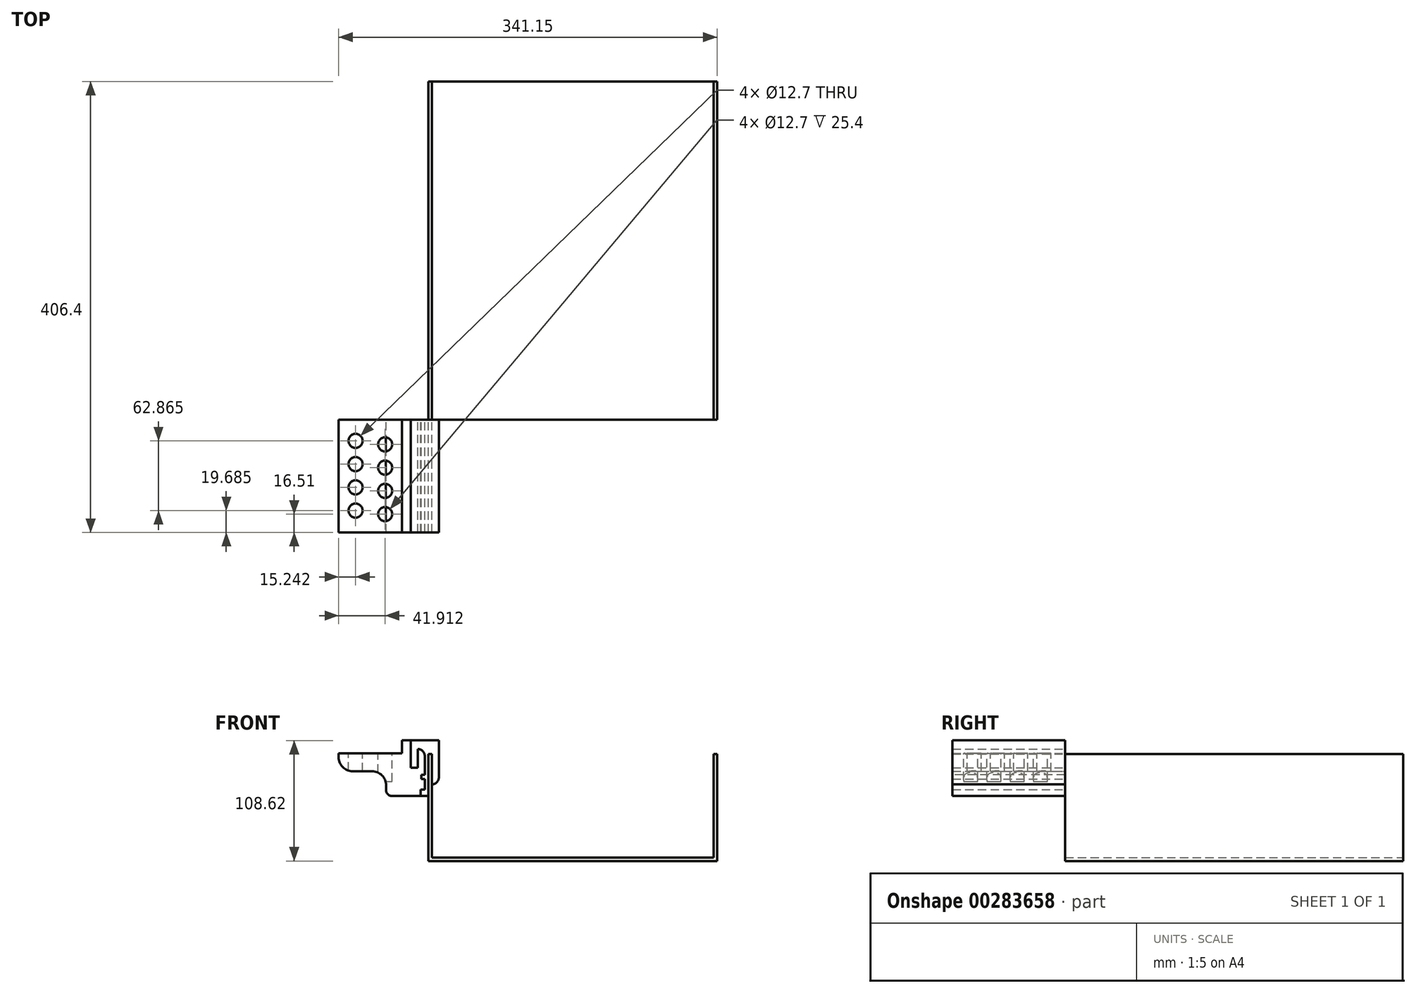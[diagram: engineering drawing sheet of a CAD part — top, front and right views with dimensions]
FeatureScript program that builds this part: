
annotation { "Feature Type Name" : "Feature", "Feature Type Description" : "" }
export const myFeature = defineFeature(function(context is Context, id is Id, definition is map)
    precondition{}
    {
        {
            var Q0;
            Q0=qCreatedBy(makeId("Front.planeOp"),FACE);
            var sketch = newSketch(context, id + "F0", { "sketchPlane" : qUnion([Q0])});
            skLineSegment(sketch, "E0", {"start": v(0, 84.47) * mm, "end": v(0, -105.43) * mm, "construction": true});
            skLineSegment(sketch, "E1", {"start": v(-72.49, 0) * mm, "end": v(75.48, 0) * mm, "construction": true});
            skLineSegment(sketch, "E2", {"start": v(-130.17, 36.54) * mm, "end": v(-130.17, -59.9) * mm});
            skLineSegment(sketch, "E3", {"start": v(-130.17, -59.9) * mm, "end": v(0, -59.9) * mm});
            skLineSegment(sketch, "E4", {"start": v(-130.17, 36.54) * mm, "end": v(-127, 36.54) * mm});
            skLineSegment(sketch, "E5", {"start": v(-127, 36.54) * mm, "end": v(-127, -56.73) * mm});
            skLineSegment(sketch, "E6", {"start": v(-127, -56.73) * mm, "end": v(0, -56.73) * mm});
            skLineSegment(sketch, "E7.MirrorCS", {"start": v(130.17, 36.54) * mm, "end": v(127, 36.54) * mm});
            skLineSegment(sketch, "E8.MirrorCS", {"start": v(130.17, -59.9) * mm, "end": v(0, -59.9) * mm});
            skLineSegment(sketch, "E9.MirrorCS", {"start": v(130.17, 36.54) * mm, "end": v(130.17, -59.9) * mm});
            skLineSegment(sketch, "E10.MirrorCS", {"start": v(127, 36.54) * mm, "end": v(127, -56.73) * mm});
            skLineSegment(sketch, "E11.MirrorCS", {"start": v(127, -56.73) * mm, "end": v(0, -56.73) * mm});
            skSolve(sketch);
        }
        {
            var Q0;
            Q0 = qSketchRegion(id + "F0", true);
            extrude(context, id + "F1", {"entities" : qUnion([Q0]), "depth" : 304.8 * mm});
        }
        {
            var Q0;
            Q0=makeQuery(id+"F1.opExtrude","CAP_FACE",FACE,{"disambiguationData":[OSD([sQuery(id+"F0.wireOp",EDGE,"E2"),sQuery(id+"F0.wireOp",EDGE,"E3"),sQuery(id+"F0.wireOp",EDGE,"E4"),sQuery(id+"F0.wireOp",EDGE,"E5"),sQuery(id+"F0.wireOp",EDGE,"E6"),sQuery(id+"F0.wireOp",EDGE,"E7.MirrorCS"),sQuery(id+"F0.wireOp",EDGE,"E8.MirrorCS"),sQuery(id+"F0.wireOp",EDGE,"E9.MirrorCS"),sQuery(id+"F0.wireOp",EDGE,"E10.MirrorCS"),sQuery(id+"F0.wireOp",EDGE,"E11.MirrorCS")])],"isStart":false});
            var sketch = newSketch(context, id + "F2", { "sketchPlane" : qUnion([Q0])});
            skLineSegment(sketch, "E12", {"start": v(-127, 9.13) * mm, "end": v(-127, 9.13) * mm});
            skLineSegment(sketch, "E13", {"start": v(-120.65, 15.48) * mm, "end": v(-120.65, 48.71) * mm});
            skLineSegment(sketch, "E14", {"start": v(-120.65, 48.71) * mm, "end": v(-146.05, 48.71) * mm});
            skLineSegment(sketch, "E15", {"start": v(-146.05, 48.71) * mm, "end": v(-146.05, 24) * mm});
            skLineSegment(sketch, "E16", {"start": v(-127, 36.54) * mm, "end": v(-127, 9.13) * mm});
            skLineSegment(sketch, "E17", {"start": v(-133.35, 34.7) * mm, "end": v(-133.35, 4.57) * mm});
            skLineSegment(sketch, "E18", {"start": v(-133.35, 4.57) * mm, "end": v(-136.96, 4.57) * mm});
            skLineSegment(sketch, "E19", {"start": v(-136.96, 4.57) * mm, "end": v(-136.96, -1.3) * mm});
            skLineSegment(sketch, "E20", {"start": v(-136.96, -1.3) * mm, "end": v(-130.17, -1.3) * mm});
            skLineSegment(sketch, "E21", {"start": v(-130.17, -1.3) * mm, "end": v(-130.17, 36.54) * mm});
            skLineSegment(sketch, "E22", {"start": v(-130.17, 36.54) * mm, "end": v(-127, 36.54) * mm});
            skLineSegment(sketch, "E23", {"start": v(-127, 36.54) * mm, "end": v(-130.17, 36.54) * mm});
            skPoint(sketch, "E24.orphan", {"position": v(-127, 41.05) * mm});
            skLineSegment(sketch, "E25", {"start": v(-130.17, 36.54) * mm, "end": v(-130.17, -1.3) * mm});
            skLineSegment(sketch, "E26", {"start": v(-146.05, 24) * mm, "end": v(-139.7, 24) * mm});
            skLineSegment(sketch, "E27", {"start": v(-139.7, 24) * mm, "end": v(-139.7, 41.05) * mm});
            skLineSegment(sketch, "E28", {"start": v(-139.7, 41.05) * mm, "end": v(-139.7, 41.05) * mm});
            skPoint(sketch, "E29.visualSharp", {"position": v(-133.35, 41.05) * mm});
            skArc(sketch, "E29.filletArc", {"start": v(-133.35, 34.7) * mm, "mid": v(-135.2, 39.2) * mm, "end": v(-139.7, 41.05) * mm});
            skPoint(sketch, "E30.visualSharp", {"position": v(-120.65, 9.13) * mm});
            skArc(sketch, "E30.filletArc", {"start": v(-127, 9.13) * mm, "mid": v(-122.5, 11) * mm, "end": v(-120.65, 15.48) * mm});
            skSolve(sketch);
        }
        {
            var Q0;
            Q0 = qSketchRegion(id + "F2", true);
            extrude(context, id + "F3", {"entities" : qUnion([Q0]), "operationType" : NewBodyOperationType.ADD, "depth" : 101.6 * mm});
        }
        {
            var Q0;
            Q0=makeQuery(id+"F3.opExtrude","SWEPT_FACE",FACE,{"disambiguationData":[OSD([sQuery(id+"F2.wireOp",EDGE,"E17")])]});
            var sketch = newSketch(context, id + "F4", { "sketchPlane" : qUnion([Q0])});
            skLineSegment(sketch, "E31.0", {"start": v(304.8, 34.7) * mm, "end": v(304.8, 4.57) * mm});
            skLineSegment(sketch, "E32.0", {"start": v(406.4, 34.7) * mm, "end": v(406.4, 4.57) * mm});
            skLineSegment(sketch, "E33", {"start": v(304.8, 19.64) * mm, "end": v(406.4, 19.64) * mm, "construction": true});
            skLineSegment(sketch, "E34.top", {"start": v(406.4, 14.1) * mm, "end": v(304.8, 14.1) * mm});
            skLineSegment(sketch, "E34.left", {"start": v(406.4, 19.64) * mm, "end": v(406.4, 14.1) * mm});
            skLineSegment(sketch, "E34.right", {"start": v(304.8, 19.64) * mm, "end": v(304.8, 14.1) * mm});
            skPoint(sketch, "E34.middle", {"position": v(355.6, 19.64) * mm});
            skLineSegment(sketch, "E35", {"start": v(304.8, 17.72) * mm, "end": v(406.4, 17.72) * mm});
            skPoint(sketch, "E34.bottom.end.orphan", {"position": v(304.8, 25.18) * mm});
            skPoint(sketch, "E36.orphan", {"position": v(406.4, 25.18) * mm});
            skLineSegment(sketch, "E37", {"start": v(304.8, 14.1) * mm, "end": v(304.8, 17.72) * mm});
            skLineSegment(sketch, "E38", {"start": v(406.4, 14.1) * mm, "end": v(406.4, 17.72) * mm});
            skSolve(sketch);
        }
        {
            var Q0;
            Q0 = qSketchRegion(id + "F4", true);
            extrude(context, id + "F5", {"entities" : qUnion([Q0]), "operationType" : NewBodyOperationType.ADD, "depth" : 3.17 * mm});
        }
        {
            var Q0;
            Q0=makeQuery(id+"F5.boolean.opBoolean","MERGE",FACE,{"derivedFrom":[makeQuery(id+"F3.opExtrude","CAP_FACE",FACE,{"disambiguationData":[OSD([sQuery(id+"F2.wireOp",EDGE,"E13"),sQuery(id+"F2.wireOp",EDGE,"E14"),sQuery(id+"F2.wireOp",EDGE,"E15"),sQuery(id+"F2.wireOp",EDGE,"E16"),sQuery(id+"F2.wireOp",EDGE,"E17"),sQuery(id+"F2.wireOp",EDGE,"E18"),sQuery(id+"F2.wireOp",EDGE,"E19"),sQuery(id+"F2.wireOp",EDGE,"E20"),sQuery(id+"F2.wireOp",EDGE,"E23"),sQuery(id+"F2.wireOp",EDGE,"E25"),sQuery(id+"F2.wireOp",EDGE,"E26"),sQuery(id+"F2.wireOp",EDGE,"E27"),sQuery(id+"F2.wireOp",EDGE,"E29.filletArc"),sQuery(id+"F2.wireOp",EDGE,"E30.filletArc")])],"isStart":true}),makeQuery(id+"F5.opExtrude","SWEPT_FACE",FACE,{"disambiguationData":[OSD([sQuery(id+"F4.wireOp",EDGE,"E37")])]})]});
            var sketch = newSketch(context, id + "F6", { "sketchPlane" : qUnion([Q0])});
            skLineSegment(sketch, "E39.0", {"start": v(139.7, 24) * mm, "end": v(139.7, 41.05) * mm});
            skLineSegment(sketch, "E40.0", {"start": v(146.05, 24) * mm, "end": v(139.7, 24) * mm});
            skLineSegment(sketch, "E41.0", {"start": v(146.05, 48.71) * mm, "end": v(146.05, 24) * mm});
            skPoint(sketch, "E42.0", {"position": v(135.2, 39.2) * mm});
            skLineSegment(sketch, "E43.0", {"start": v(133.35, 34.7) * mm, "end": v(133.35, 17.72) * mm});
            skPoint(sketch, "E44.0", {"position": v(134.94, 17.72) * mm});
            skLineSegment(sketch, "E45.0", {"start": v(136.53, 17.72) * mm, "end": v(133.35, 17.72) * mm});
            skLineSegment(sketch, "E46.0", {"start": v(136.53, 17.72) * mm, "end": v(136.53, 14.1) * mm});
            skLineSegment(sketch, "E47.0", {"start": v(136.53, 14.1) * mm, "end": v(133.35, 14.1) * mm});
            skLineSegment(sketch, "E48.0", {"start": v(133.35, 14.1) * mm, "end": v(133.35, 4.57) * mm});
            skLineSegment(sketch, "E49.0", {"start": v(133.35, 4.57) * mm, "end": v(136.96, 4.57) * mm});
            skLineSegment(sketch, "E50.0", {"start": v(136.96, 4.57) * mm, "end": v(136.96, -1.3) * mm});
            skArc(sketch, "E51.0", {"start": v(133.35, 34.7) * mm, "mid": v(135.2, 39.2) * mm, "end": v(139.7, 41.05) * mm});
            skLineSegment(sketch, "E52", {"start": v(133.35, 41.05) * mm, "end": v(133.35, 17.72) * mm});
            skLineSegment(sketch, "E53", {"start": v(136.55, 17.78) * mm, "end": v(136.53, 14.1) * mm});
            skLineSegment(sketch, "E54", {"start": v(136.96, -1.3) * mm, "end": v(168.12, -1.3) * mm});
            skLineSegment(sketch, "E55", {"start": v(210.97, 33.68) * mm, "end": v(210.97, 37.28) * mm});
            skLineSegment(sketch, "E56", {"start": v(210.97, 37.28) * mm, "end": v(153.82, 37.28) * mm});
            skLineSegment(sketch, "E57", {"start": v(153.82, 37.28) * mm, "end": v(153.82, 48.71) * mm});
            skLineSegment(sketch, "E58", {"start": v(153.82, 48.71) * mm, "end": v(146.05, 48.71) * mm});
            skLineSegment(sketch, "E59", {"start": v(139.7, 41.05) * mm, "end": v(133.35, 41.05) * mm});
            skPoint(sketch, "E60.visualSharp", {"position": v(210.97, -1.3) * mm});
            skLineSegment(sketch, "E61", {"start": v(198.27, 20.98) * mm, "end": v(180.82, 20.98) * mm});
            skLineSegment(sketch, "E62", {"start": v(168.12, 8.28) * mm, "end": v(168.12, -1.3) * mm});
            skPoint(sketch, "E63.visualSharp", {"position": v(168.12, 20.98) * mm});
            skArc(sketch, "E63.filletArc", {"start": v(180.82, 20.98) * mm, "mid": v(171.84, 17.26) * mm, "end": v(168.12, 8.28) * mm});
            skPoint(sketch, "E64.visualSharp", {"position": v(210.97, 20.98) * mm});
            skArc(sketch, "E64.filletArc", {"start": v(198.27, 20.98) * mm, "mid": v(207.25, 24.7) * mm, "end": v(210.97, 33.68) * mm});
            skSolve(sketch);
        }
        {
            var Q0;
            Q0=makeQuery(id+"F6.imprint","IMPRINT",FACE,{"disambiguationData":[TD([[makeQuery(id+"F6.imprint","IMPRINT",EDGE,{"derivedFrom":sQuery(id+"F6.wireOp",EDGE,"E40.0")}),1.0]])]});
            extrude(context, id + "F7", {"entities" : qUnion([Q0]), "oppositeDirection" : true, "depth" : 101.6 * mm});
        }
        {
            var Q0;
            Q0=makeQuery(id+"F7.opExtrude","SWEPT_FACE",FACE,{"disambiguationData":[OSD([sQuery(id+"F6.wireOp",EDGE,"E56")])]});
            var sketch = newSketch(context, id + "F8", { "sketchPlane" : qUnion([Q0])});
            skLineSegment(sketch, "E65", {"start": v(-182.4, -304.8) * mm, "end": v(-182.4, -406.4) * mm, "construction": true});
            skCircle(sketch, "E66", {"center": v(-195.73, -323.85) * mm, "radius": 6.35 * mm});
            skCircle(sketch, "E67", {"center": v(-195.73, -344.8) * mm, "radius": 6.35 * mm});
            skCircle(sketch, "E68", {"center": v(-195.73, -365.76) * mm, "radius": 6.35 * mm});
            skCircle(sketch, "E69", {"center": v(-195.73, -386.72) * mm, "radius": 6.35 * mm});
            skCircle(sketch, "E70.MirrorC", {"center": v(-169.06, -327.03) * mm, "radius": 6.35 * mm});
            skCircle(sketch, "E71.MirrorC", {"center": v(-169.06, -347.98) * mm, "radius": 6.35 * mm});
            skCircle(sketch, "E72.MirrorC", {"center": v(-169.06, -368.94) * mm, "radius": 6.35 * mm});
            skCircle(sketch, "E73.MirrorC", {"center": v(-169.06, -389.9) * mm, "radius": 6.35 * mm});
            skSolve(sketch);
        }
        {
            var Q0;
            Q0 = qSketchRegion(id + "F8", true);
            extrude(context, id + "F9", {"entities" : qUnion([Q0]), "operationType" : NewBodyOperationType.REMOVE, "oppositeDirection" : true, "depth" : 25.4 * mm});
        }
        {
            var Q0;
            Q0=makeQuery(id+"F7.opExtrude","SWEPT_EDGE",EDGE,{"disambiguationData":[OSD([sQuery(id+"F6.wireOp",EDGE,"E54"),sQuery(id+"F6.wireOp",EDGE,"E62")])]});
            fillet(context, id + "F10", {"entities" : qUnion([Q0]), "radius" : 5.08 * mm, "tangentPropagation" : true, "allowEdgeOverflow" : false});
        }
    });
